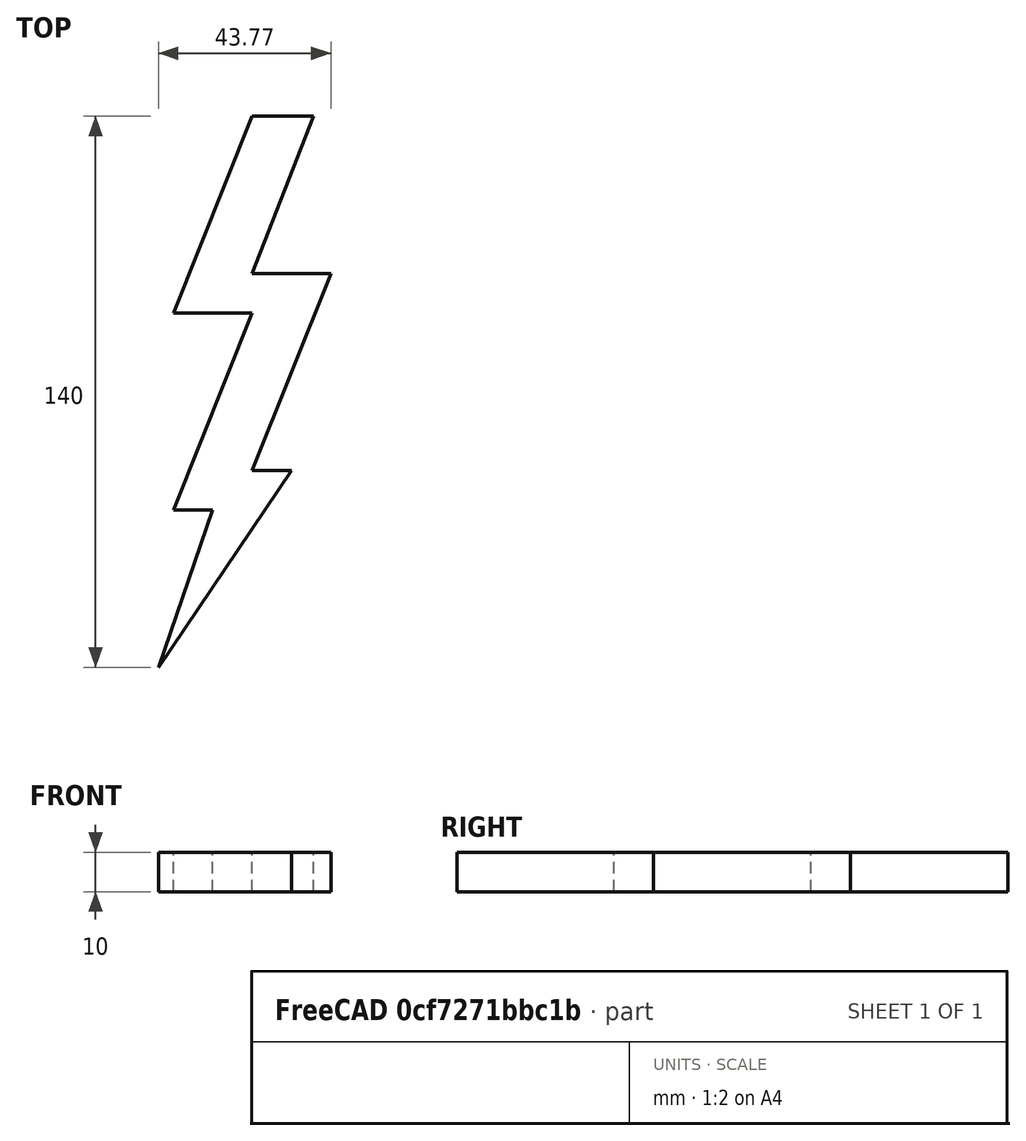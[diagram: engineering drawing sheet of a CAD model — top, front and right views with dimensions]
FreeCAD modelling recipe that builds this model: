
FCSTD DOCUMENT  (FreeCAD 0.18.4R)
Label: tutorial_freecad_ex16_d
License: All rights reserved
LicenseURL: http://en.wikipedia.org/wiki/All_rights_reserved
objects: Sketcher::SketchObject×1, PartDesign::Pad×1, PartDesign::Body×1
note: 4 computed .brp shape members not serialized (recipe doc carries the construction recipe); baked Part::Feature solids carry a one-line shape summary decoded from their .brp

FEATURE [Sketcher::SketchObject] Sketch  label="boceto_rayo"
  MapMode = 5
  Support = -> [XY_Plane]
  sketch-geometry (11):
    g0: LineSegment StartX=40 StartY=70 StartZ=0 EndX=20 EndY=20 EndZ=0
    g1: LineSegment StartX=20 StartY=20 StartZ=0 EndX=40 EndY=20 EndZ=0
    g2: LineSegment StartX=40 StartY=20 StartZ=0 EndX=20 EndY=-30 EndZ=0
    g3: LineSegment StartX=20 StartY=-30 StartZ=0 EndX=30 EndY=-30 EndZ=0
    g4: LineSegment StartX=30 StartY=-30 StartZ=0 EndX=16.2285 EndY=-70 EndZ=0
    g5: LineSegment StartX=16.2285 StartY=-70 StartZ=0 EndX=50 EndY=-20 EndZ=0
    g6: LineSegment StartX=50 StartY=-20 StartZ=0 EndX=40 EndY=-20 EndZ=0
    g7: LineSegment StartX=40 StartY=-20 StartZ=0 EndX=60 EndY=30 EndZ=0
    g8: LineSegment StartX=60 StartY=30 StartZ=0 EndX=40 EndY=30 EndZ=0
    g9: LineSegment StartX=40 StartY=30 StartZ=0 EndX=55.6481 EndY=70 EndZ=0
    g10: LineSegment StartX=55.6481 StartY=70 StartZ=0 EndX=40 EndY=70 EndZ=0
  constraints (11):
    c: Coincident(g0,g1)
    c: Coincident(g1,g2)
    c: Coincident(g2,g3)
    c: Coincident(g3,g4)
    c: Coincident(g4,g5)
    c: Coincident(g5,g6)
    c: Coincident(g6,g7)
    c: Coincident(g7,g8)
    c: Coincident(g8,g9)
    c: Coincident(g9,g10)
    c: Coincident(g10,g0)
FEATURE [PartDesign::Pad] Pad  label="pad_rayo"
  Length = 10
  Length2 = 100
  Profile = -> Sketch
  Refine = true
  Type = 0
FEATURE [PartDesign::Body] Body  label="rayo"
  Group = -> [Sketch,Pad]
  Origin = -> Origin
  Tip = -> Pad
